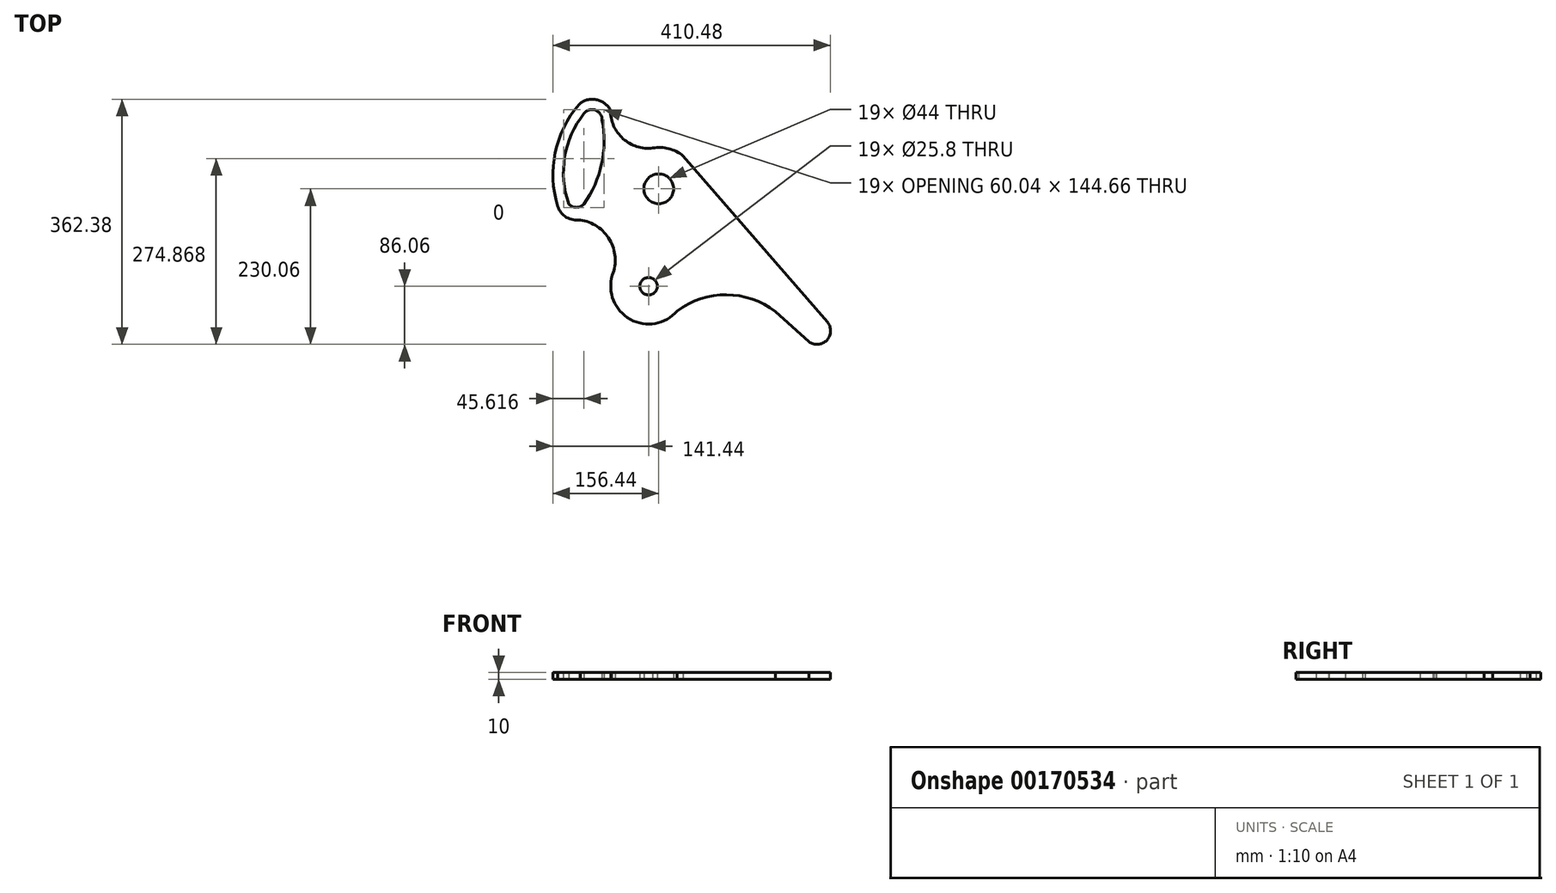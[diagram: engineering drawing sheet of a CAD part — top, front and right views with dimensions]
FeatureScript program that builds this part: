
annotation { "Feature Type Name" : "Feature", "Feature Type Description" : "" }
export const myFeature = defineFeature(function(context is Context, id is Id, definition is map)
    precondition{}
    {
        {
            var Q0;
            Q0=qCreatedBy(makeId("Top.planeOp"),FACE);
            var sketch = newSketch(context, id + "F0", { "sketchPlane" : qUnion([Q0])});
            skCircle(sketch, "E0", {"center": v(0, 0) * mm, "radius": 22 * mm});
            skCircle(sketch, "E1", {"center": v(0, 0) * mm, "radius": 42 * mm});
            skCircle(sketch, "E2", {"center": v(-15, -144) * mm, "radius": 12.9 * mm});
            skCircle(sketch, "E3", {"center": v(-15, -144) * mm, "radius": 56 * mm});
            skArc(sketch, "E4", {"start": v(-68.53, -127.56) * mm, "mid": v(-72.55, -75.31) * mm, "end": v(-116.08, -46.15) * mm});
            skArc(sketch, "E5", {"start": v(-149.37, -25.83) * mm, "mid": v(-136.48, -42.13) * mm, "end": v(-116.08, -46.15) * mm});
            skArc(sketch, "E6", {"start": v(-117.87, 124.86) * mm, "mid": v(-153.07, 53.58) * mm, "end": v(-149.37, -25.83) * mm});
            skArc(sketch, "E7", {"start": v(-71.43, 116.1) * mm, "mid": v(-92.52, 131.8) * mm, "end": v(-117.87, 124.86) * mm});
            skArc(sketch, "E8", {"start": v(-71.43, 116.1) * mm, "mid": v(-52.76, 74.07) * mm, "end": v(-8.9, 60.2) * mm});
            skArc(sketch, "E9", {"start": v(36.2, 48.55) * mm, "mid": v(14.9, 59.24) * mm, "end": v(-8.9, 60.2) * mm});
            skLineSegment(sketch, "E10", {"start": v(36.2, 48.55) * mm, "end": v(249.15, -196.95) * mm});
            skArc(sketch, "E11", {"start": v(221.83, -225.9) * mm, "mid": v(248.59, -223.78) * mm, "end": v(249.15, -196.95) * mm});
            skLineSegment(sketch, "E12", {"start": v(249.15, -196.95) * mm, "end": v(168.27, -123.86) * mm});
            skLineSegment(sketch, "E13", {"start": v(221.83, -225.9) * mm, "end": v(140.92, -153.05) * mm});
            skArc(sketch, "E14", {"start": v(168.27, -123.86) * mm, "mid": v(140.26, -125.03) * mm, "end": v(140.92, -153.05) * mm});
            skArc(sketch, "E15", {"start": v(172.73, -181.68) * mm, "mid": v(100.2, -156.64) * mm, "end": v(27.33, -180.66) * mm});
            skArc(sketch, "E16", {"start": v(-110.73, 111.17) * mm, "mid": v(-139.07, 47.1) * mm, "end": v(-132.83, -22.66) * mm});
            skArc(sketch, "E17", {"start": v(-132.83, -22.66) * mm, "mid": v(-121.78, -27.52) * mm, "end": v(-110.73, -22.66) * mm});
            skArc(sketch, "E18", {"start": v(-110.73, -22.66) * mm, "mid": v(-84.46, 36.63) * mm, "end": v(-83.76, 101.48) * mm});
            skArc(sketch, "E19", {"start": v(-83.76, 101.48) * mm, "mid": v(-93.68, 116.26) * mm, "end": v(-110.73, 111.17) * mm});
            skSolve(sketch);
        }
        {
            var Q0;
            Q0=makeQuery(id+"F0.imprint","IMPRINT",FACE,{"disambiguationData":[TD([[makeQuery(id+"F0.imprint","IMPRINT",EDGE,{"derivedFrom":sQuery(id+"F0.wireOp",EDGE,"E1")}),-1.0]])]});
            var Q1;
            Q1=makeQuery(id+"F0.imprint","IMPRINT",FACE,{"disambiguationData":[TD([[makeQuery(id+"F0.imprint","IMPRINT",EDGE,{"derivedFrom":sQuery(id+"F0.wireOp",EDGE,"E0")}),-1.0]])]});
            var Q2;
            Q2=makeQuery(id+"F0.imprint","IMPRINT",FACE,{"disambiguationData":[TD([[makeQuery(id+"F0.imprint","IMPRINT",EDGE,{"derivedFrom":sQuery(id+"F0.wireOp",EDGE,"E2")}),-1.0]])]});
            var Q3;
            {var subQ3=sQuery(id+"F0.wireOp",EDGE,"E11");Q3=makeQuery(id+"F0.imprint","IMPRINT",FACE,{"disambiguationData":[TD([[makeQuery(id+"F0.imprint","IMPRINT",EDGE,{"derivedFrom":subQ3}),1.0]])]});}
            extrude(context, id + "F1", {"entities" : qUnion([Q0, Q1, Q2, Q3]), "depth" : 10 * mm});
        }
    });
